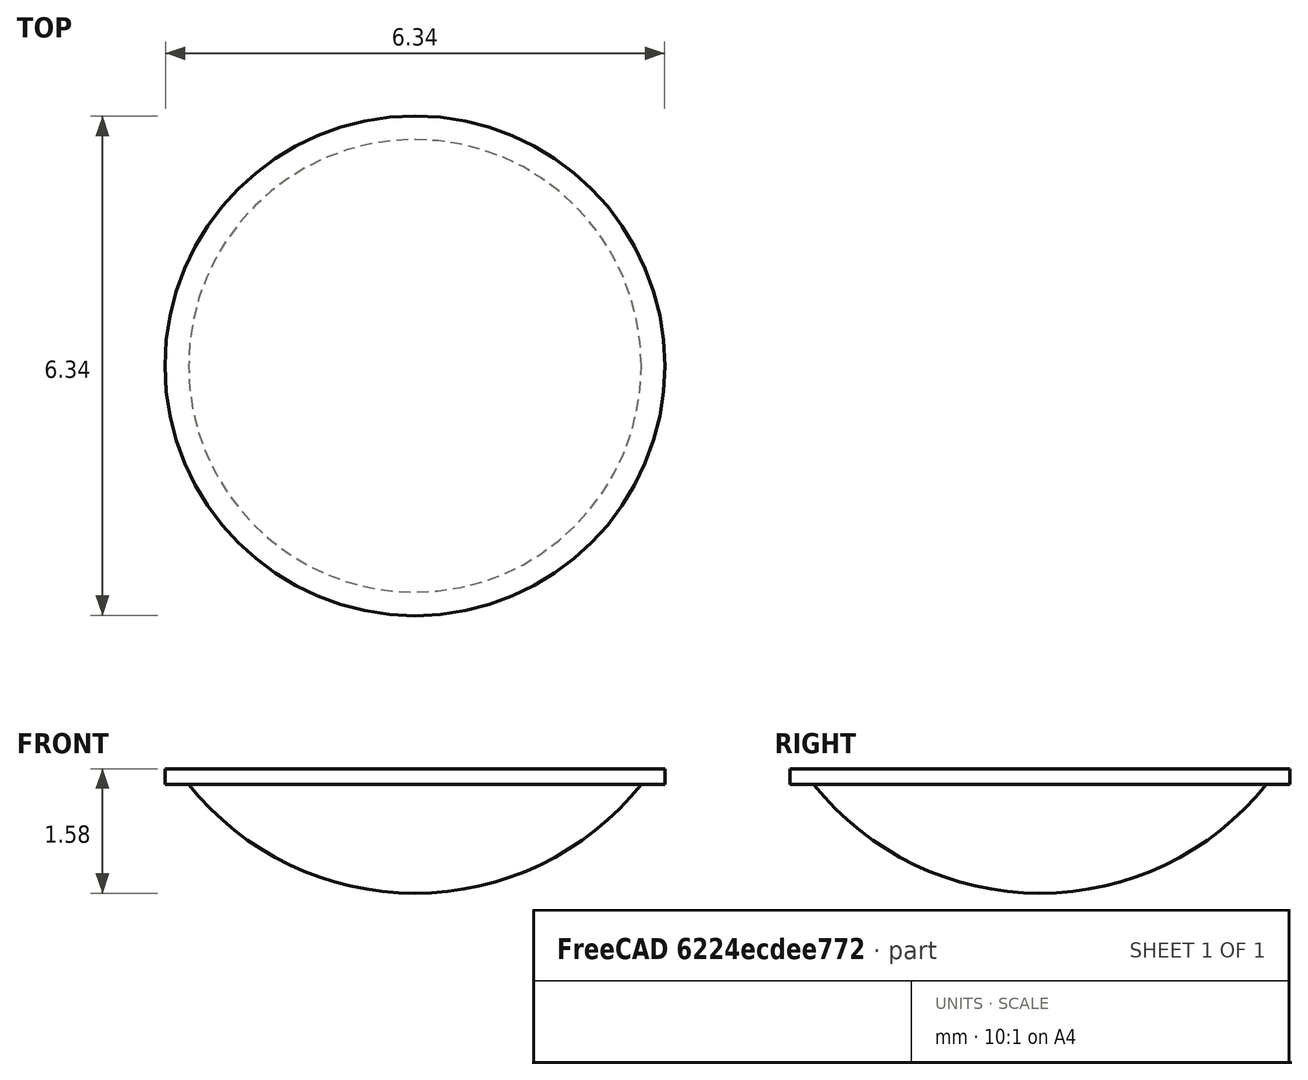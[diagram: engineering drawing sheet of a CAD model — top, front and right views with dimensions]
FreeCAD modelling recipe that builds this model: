
FCSTD DOCUMENT  (FreeCAD 0.18R15969 (Git))
Label: rubber_dome
License: All rights reserved
LicenseURL: http://en.wikipedia.org/wiki/All_rights_reserved
objects: Sketcher::SketchObject×1, PartDesign::Revolution×1, PartDesign::Body×1
note: 4 computed .brp shape members not serialized (recipe doc carries the construction recipe); baked Part::Feature solids carry a one-line shape summary decoded from their .brp

FEATURE [Sketcher::SketchObject] Sketch
  MapMode = 5
  Placement = pos=(0,0,0) rot=(1,0,0;1.5708rad)
  Support = -> [XZ_Plane]
  sketch-geometry (5):
    g0: LineSegment StartX=0 StartY=0 StartZ=0 EndX=-3.175 EndY=0 EndZ=0
    g1: LineSegment StartX=-3.175 StartY=0 StartZ=0 EndX=-3.175 EndY=-0.2 EndZ=0
    g2: LineSegment StartX=-3.175 StartY=-0.2 StartZ=0 EndX=-2.875 EndY=-0.2 EndZ=0
    g3: ArcOfCircle CenterX=0 CenterY=2.10479 CenterZ=0 NormalX=0 NormalY=0 NormalZ=1 AngleXU=0 Radius=3.68479 StartAngle=3.81735 EndAngle=4.71239
    g4: LineSegment StartX=0 StartY=-1.58 StartZ=0 EndX=0 EndY=0 EndZ=0
  constraints (15):
    c: Coincident(g0,g-1)
    c: PointOnObject(g0,g-1)
    c: Coincident(g1,g0)
    c: Coincident(g2,g1)
    c: Horizontal(g2)
    c: DistanceX(g0,g0) = 3.175
    c: Vertical(g1)
    c: DistanceY(g1,g1) = 0.2
    c: Coincident(g3,g2)
    c: PointOnObject(g3,g-2)
    c: Coincident(g4,g3)
    c: Coincident(g4,g0)
    c: DistanceY(g4,g4) = 1.58
    c: DistanceX(g1,g2) = 0.3
    c: PointOnObject(g3,g-2)
FEATURE [PartDesign::Revolution] Revolution
  Angle = 360
  Axis = (0,2e-16,1)
  Base = (0,0,0)
  Placement = pos=(0,0,0) rot=(1,0,0;1.5708rad)
  Profile = -> Sketch
  ReferenceAxis = -> Sketch [V_Axis]
  Refine = true
FEATURE [PartDesign::Body] Body
  Group = -> [Sketch,Revolution]
  Origin = -> Origin
  Tip = -> Revolution
